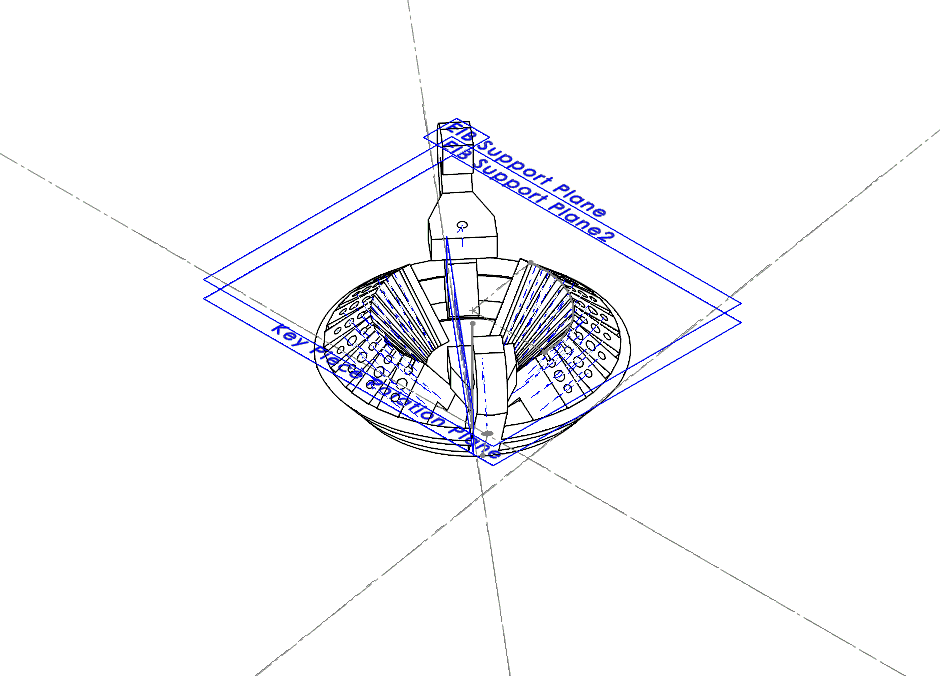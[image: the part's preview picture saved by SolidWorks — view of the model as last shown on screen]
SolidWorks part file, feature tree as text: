
SOLIDWORKS PART (.sldprt)
format: sldprt  version: not decoded by parser v0  size: 931,840 bytes
history: native  units: mm
features: sketch x14, plane x4, extrude x2, fillet x2, hole x2, material x1, cut_extrude x1, revolve x1, mirror x1 (+12 scaffold rows collapsed)
feature tree (40):
  scaffold x12  (default folders/planes/origin — collapsed)
  material  "Material <not specified>"
  sketch  "Sketch3"
  sketch  "KeyPieceSketch"  dims[c1.D1=10.0mm c1.D2=7.0mm c1.D3=1.5mm c1.D4=1.0mm c1.D5=4.5mm c1.D6=1.75mm c1.D7=3.5mm c1.D8=3.0mm c1.D9=10.0mm c1.D10=~7.071068mm c1.D11=~785.398163mm c2.D6=1.75mm c2.D10=~11.706686mm c2.D11=~17.068997mm c2.D1=~263.580812mm]
  extrude  "Key Piece"  Depth=1.5mm
  plane  "Key Piece Rotation Plane"
  sketch  "Key Piece Rotation Arc"  dims[c1.D2=~11.706686mm c1.D1=~349.06585mm c2.D2=~349.06585mm c2.D1=~2792.526803mm c3.D2=~1745.329252mm]
  sketch  "Cone Inside"  dims[c1.D1=7.0mm c2.D1=8.0 c2.D3=10.0mm c2.D2=1.0 c2.D4=10.0mm]
  sketch  "Sketch27"  dims[D1=0.0mm]
  cut_extrude  "Tubing Holes"  [1 undecoded]
  sketch  "Sketch36"  dims[c1.D2=1.0mm c1.D1=0.5mm c2.D2=1.5mm]
  sketch  "Outer Cone Spacer"  dims[D1=1.5mm D2=2.0mm D3=2.0mm ConeBaseRadius=~13.71855mm]
  revolve  "Outer Cone Spacer Revolve"  [1 undecoded]
  sketch  "Support Plane Axis"  dims[D1=~1458.596589mm]
  extrude  "CrvPattern2"  Depth=8
  plane  "Support Plane"
  mirror  "Mirror1"
  sketch  "Sketch30"  dims[c1.D1=20.0mm c1.D2=30.0mm c2.D1=27.0mm c2.D3=~785.398163mm c2.D2=12.0mm c2.D4=~698.131701mm c2.D5=~1570.796327mm c2.D6=~16.410183mm c3.D4=~698.131701mm c3.D1=5.0mm c3.D2=5.0mm c3.D3=4.0mm c4.D1=1.75mm c4.D2=1.75mm]
  fillet  "Fillet1"  Radius=4mm
  plane  "EIB Support Plane"  Offset=0mm
  plane  "EIB Support Plane2"  Offset=19mm
  sketch  "Sketch37"  dims[c1.D1=29.5mm c1.D2=7.62mm c1.D3=4.0mm c2.D1=3.0mm]
  sketch  "Sketch35"  dims[D3=1.2mm D4=1.2mm D1=7.5mm D2=13.335mm]
  sketch  "Sketch38"  dims[D2=~1.419292mm D1=~4.242336mm]
  sketch  "Sketch39"  dims[D2=~2.471205mm D1=~5.325605mm]
  fillet  "Fillet2"  Radius=2mm
  hole  "Cone Mounting Hole"  [1 undecoded]
  hole  "Cone Mounting Hole 2"  [1 undecoded]
  sketch  "ConeRevolve"  dims[c1.D1=~9.137851mm c1.D2=~872.664626mm c2.D1=~6283.185307mm c2.D3=10.0mm c2.D4=1.0mm c2.D7=0.0mm]
decode coverage: 17 of 23 modeling features carry decoded parameters
note: ~ marks probable driven/reference dimensions
note: 4 parameter values undecoded
summary: no parameter record found for 4 features
note: suppression state not decoded; provenance and decode notes live in map.json
